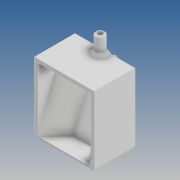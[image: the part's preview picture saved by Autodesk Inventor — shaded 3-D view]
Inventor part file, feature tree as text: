
AUTODESK INVENTOR PART (.ipt)
format: ipt  version: 2020 (Build 240168000, 168)  size: 400,384 bytes
history: native  units: mm
features: extrude x6, chamfer x5, sketch x5, fillet x2, other x1
ambient origin geometry x8: Origin, YZ Plane, XZ Plane, XY Plane, X Axis, Y Axis, Z Axis, Center Point
bodies: Body1 (feature_tree)
feature tree (19):
  other  "솔리드1"
  extrude  "돌출1"  Depth=17.0mm
  extrude  "돌출2"  Depth=20.0mm
  extrude  "돌출3"  Depth=1.5mm TaperAngle=0.0deg
  fillet  "모깎기1"  Radius=1.0mm
  chamfer  "모따기1"  Distance=10.0mm
  chamfer  "모따기2"  Distance=13.0mm
  chamfer  "모따기3"  Distance=5.0mm
  extrude  "돌출4"  Depth=2.0mm
  extrude  "돌출5"  Depth=2.0mm
  chamfer  "모따기4"  Distance=10.0mm
  extrude  "돌출6"  Depth=1.0mm
  chamfer  "모따기5"  Distance=5.0mm Angle=45.0deg
  fillet  "모깎기3"  Radius=5.0mm
  sketch  "스케치1"
  sketch  "스케치2"
  sketch  "스케치3"
  sketch  "스케치4"
  sketch  "스케치6"
